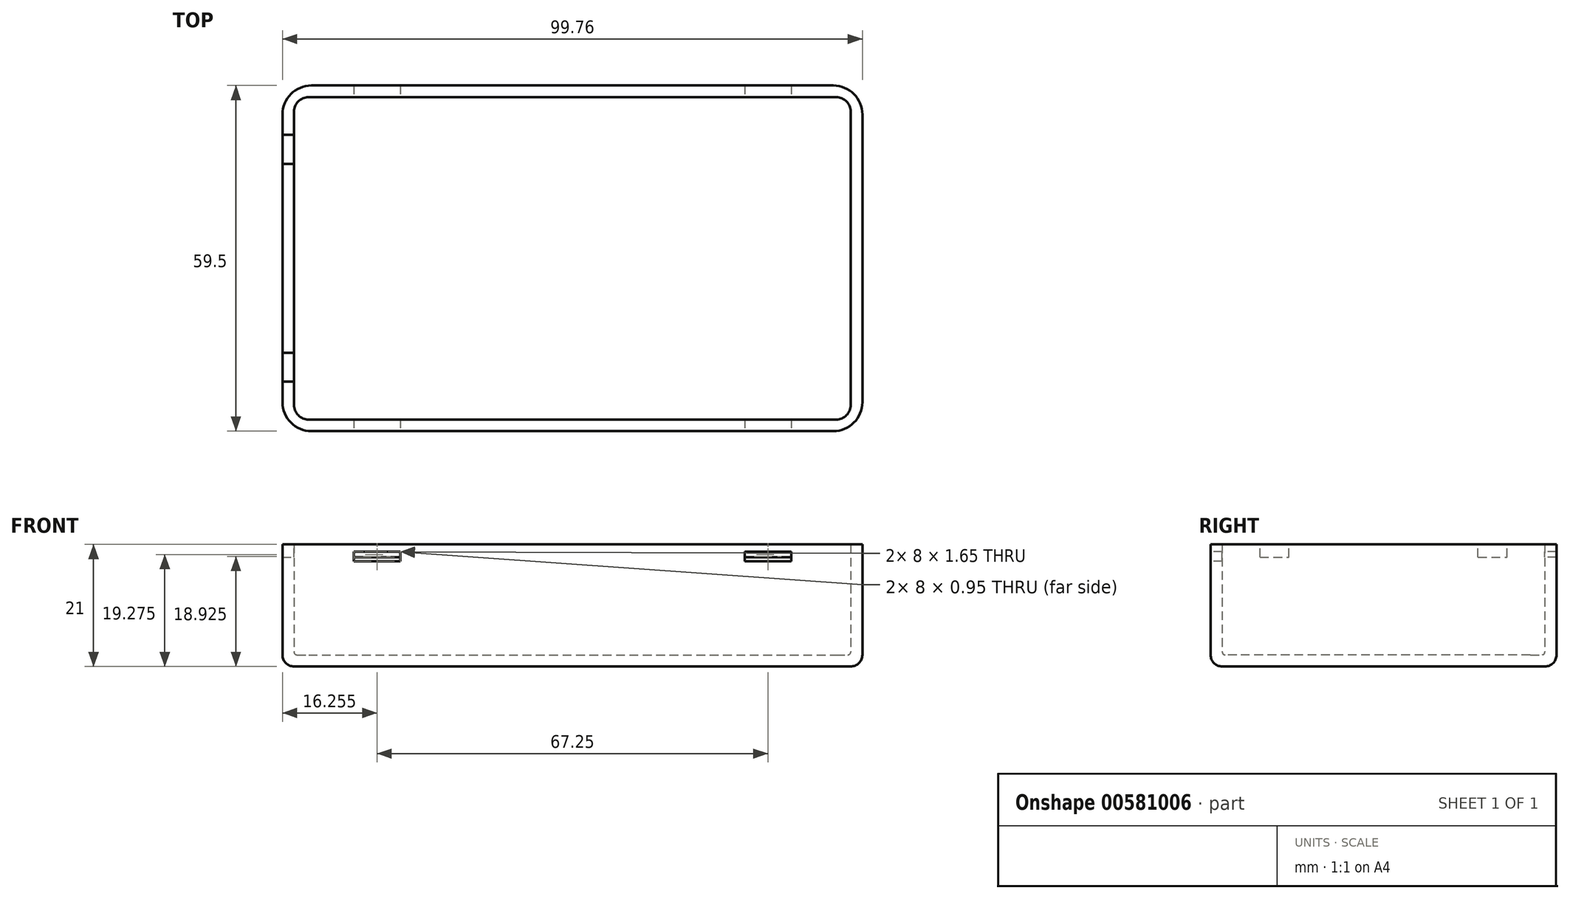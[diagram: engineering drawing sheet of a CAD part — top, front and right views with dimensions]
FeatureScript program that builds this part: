
annotation { "Feature Type Name" : "Feature", "Feature Type Description" : "" }
export const myFeature = defineFeature(function(context is Context, id is Id, definition is map)
    precondition{}
    {
        {
            var Q0;
            Q0=qCreatedBy(makeId("Top.planeOp"),FACE);
            var sketch = newSketch(context, id + "F0", { "sketchPlane" : qUnion([Q0])});
            skLineSegment(sketch, "E0.bottom", {"start": v(44.88, -29.75) * mm, "end": v(-44.88, -29.75) * mm});
            skLineSegment(sketch, "E0.top", {"start": v(44.88, 29.75) * mm, "end": v(-44.88, 29.75) * mm});
            skLineSegment(sketch, "E0.left", {"start": v(49.88, -24.75) * mm, "end": v(49.88, 24.75) * mm});
            skLineSegment(sketch, "E0.right", {"start": v(-49.88, -24.75) * mm, "end": v(-49.88, 24.75) * mm});
            skPoint(sketch, "E0.middle", {"position": v(0, 0) * mm});
            skLineSegment(sketch, "E1.bottom", {"start": v(45.38, -27.75) * mm, "end": v(-45.38, -27.75) * mm});
            skLineSegment(sketch, "E1.top", {"start": v(45.38, 27.75) * mm, "end": v(-45.38, 27.75) * mm});
            skLineSegment(sketch, "E1.left", {"start": v(47.88, -25.25) * mm, "end": v(47.88, 25.25) * mm});
            skLineSegment(sketch, "E1.right", {"start": v(-47.88, -25.25) * mm, "end": v(-47.88, 25.25) * mm});
            skPoint(sketch, "E2.visualSharp", {"position": v(-49.88, 29.75) * mm});
            skArc(sketch, "E2.filletArc", {"start": v(-44.88, 29.75) * mm, "mid": v(-48.41, 28.29) * mm, "end": v(-49.88, 24.75) * mm});
            skPoint(sketch, "E3.visualSharp", {"position": v(-49.88, -29.75) * mm});
            skArc(sketch, "E3.filletArc", {"start": v(-49.88, -24.75) * mm, "mid": v(-48.41, -28.29) * mm, "end": v(-44.88, -29.75) * mm});
            skPoint(sketch, "E4.visualSharp", {"position": v(49.88, 29.75) * mm});
            skArc(sketch, "E4.filletArc", {"start": v(49.87, 24.75) * mm, "mid": v(48.41, 28.29) * mm, "end": v(44.88, 29.75) * mm});
            skPoint(sketch, "E5.visualSharp", {"position": v(49.88, -29.75) * mm});
            skArc(sketch, "E5.filletArc", {"start": v(44.88, -29.75) * mm, "mid": v(48.41, -28.29) * mm, "end": v(49.88, -24.75) * mm});
            skPoint(sketch, "E6.visualSharp", {"position": v(-47.88, 27.75) * mm});
            skArc(sketch, "E6.filletArc", {"start": v(-45.38, 27.75) * mm, "mid": v(-47.14, 27.02) * mm, "end": v(-47.88, 25.25) * mm});
            skPoint(sketch, "E7.visualSharp", {"position": v(47.88, 27.75) * mm});
            skArc(sketch, "E7.filletArc", {"start": v(47.88, 25.25) * mm, "mid": v(47.14, 27.02) * mm, "end": v(45.38, 27.75) * mm});
            skPoint(sketch, "E8.visualSharp", {"position": v(47.88, -27.75) * mm});
            skArc(sketch, "E8.filletArc", {"start": v(45.38, -27.75) * mm, "mid": v(47.14, -27.02) * mm, "end": v(47.88, -25.25) * mm});
            skPoint(sketch, "E9.visualSharp", {"position": v(-47.88, -27.75) * mm});
            skArc(sketch, "E9.filletArc", {"start": v(-47.88, -25.25) * mm, "mid": v(-47.14, -27.02) * mm, "end": v(-45.38, -27.75) * mm});
            skSolve(sketch);
        }
        {
            var Q0;
            Q0=makeQuery(id+"F0.imprint","IMPRINT",FACE,{"disambiguationData":[TD([[makeQuery(id+"F0.imprint","IMPRINT",EDGE,{"derivedFrom":sQuery(id+"F0.wireOp",EDGE,"E0.bottom")}),-1.0]])]});
            var Q1;
            Q1=makeQuery(id+"F0.imprint","IMPRINT",FACE,{"disambiguationData":[TD([[makeQuery(id+"F0.imprint","IMPRINT",EDGE,{"derivedFrom":sQuery(id+"F0.wireOp",EDGE,"E1.bottom")}),-1.0]])]});
            extrude(context, id + "F1", {"entities" : qUnion([Q0, Q1]), "depth" : 2 * mm, "offsetDistance" : 25 * mm});
        }
        {
            var Q0;
            Q0 = qSketchRegion(id + "F0", true);
            extrude(context, id + "F2", {"entities" : qUnion([Q0]), "operationType" : NewBodyOperationType.ADD, "depth" : 21 * mm, "offsetDistance" : 25 * mm});
        }
        {
            var Q0;
            Q0=makeQuery(id+"F1.opExtrude","CAP_EDGE",EDGE,{"disambiguationData":[OSD([sQuery(id+"F0.wireOp",EDGE,"E0.bottom")])],"isStart":true});
            var Q1;
            Q1=makeQuery(id+"F1.opExtrude","CAP_EDGE",EDGE,{"disambiguationData":[OSD([sQuery(id+"F0.wireOp",EDGE,"E3.filletArc")])],"isStart":true});
            var Q2;
            Q2=makeQuery(id+"F1.opExtrude","CAP_EDGE",EDGE,{"disambiguationData":[OSD([sQuery(id+"F0.wireOp",EDGE,"E0.right")])],"isStart":true});
            var Q3;
            Q3=makeQuery(id+"F1.opExtrude","CAP_EDGE",EDGE,{"disambiguationData":[OSD([sQuery(id+"F0.wireOp",EDGE,"E2.filletArc")])],"isStart":true});
            var Q4;
            Q4=makeQuery(id+"F1.opExtrude","CAP_EDGE",EDGE,{"disambiguationData":[OSD([sQuery(id+"F0.wireOp",EDGE,"E0.top")])],"isStart":true});
            var Q5;
            Q5=makeQuery(id+"F1.opExtrude","CAP_EDGE",EDGE,{"disambiguationData":[OSD([sQuery(id+"F0.wireOp",EDGE,"E4.filletArc")])],"isStart":true});
            var Q6;
            Q6=makeQuery(id+"F1.opExtrude","CAP_EDGE",EDGE,{"disambiguationData":[OSD([sQuery(id+"F0.wireOp",EDGE,"E0.left")])],"isStart":true});
            var Q7;
            Q7=makeQuery(id+"F1.opExtrude","CAP_EDGE",EDGE,{"disambiguationData":[OSD([sQuery(id+"F0.wireOp",EDGE,"E5.filletArc")])],"isStart":true});
            fillet(context, id + "F3", {"entities" : qUnion([Q0, Q1, Q2, Q3, Q4, Q5, Q6, Q7]), "radius" : 2 * mm, "tangentPropagation" : true, "allowEdgeOverflow" : false});
        }
        {
            var Q0;
            Q0=makeQuery(id+"F2.opExtrude","CAP_FACE",FACE,{"disambiguationData":[OSD([sQuery(id+"F0.wireOp",EDGE,"E0.bottom"),sQuery(id+"F0.wireOp",EDGE,"E0.top"),sQuery(id+"F0.wireOp",EDGE,"E0.left"),sQuery(id+"F0.wireOp",EDGE,"E0.right"),sQuery(id+"F0.wireOp",EDGE,"E1.bottom"),sQuery(id+"F0.wireOp",EDGE,"E1.top"),sQuery(id+"F0.wireOp",EDGE,"E1.left"),sQuery(id+"F0.wireOp",EDGE,"E1.right"),sQuery(id+"F0.wireOp",EDGE,"E2.filletArc"),sQuery(id+"F0.wireOp",EDGE,"E3.filletArc"),sQuery(id+"F0.wireOp",EDGE,"E4.filletArc"),sQuery(id+"F0.wireOp",EDGE,"E5.filletArc"),sQuery(id+"F0.wireOp",EDGE,"E6.filletArc"),sQuery(id+"F0.wireOp",EDGE,"E7.filletArc"),sQuery(id+"F0.wireOp",EDGE,"E8.filletArc"),sQuery(id+"F0.wireOp",EDGE,"E9.filletArc")])],"isStart":false});
            var sketch = newSketch(context, id + "F4", { "sketchPlane" : qUnion([Q0])});
            skLineSegment(sketch, "E10.bottom", {"start": v(-49.88, 21.25) * mm, "end": v(-47.88, 21.25) * mm});
            skLineSegment(sketch, "E10.top", {"start": v(-49.88, 16.25) * mm, "end": v(-47.88, 16.25) * mm});
            skLineSegment(sketch, "E10.left", {"start": v(-49.88, 21.25) * mm, "end": v(-49.88, 16.25) * mm});
            skLineSegment(sketch, "E10.right", {"start": v(-47.88, 21.25) * mm, "end": v(-47.88, 16.25) * mm});
            skLineSegment(sketch, "E11.bottom", {"start": v(-49.88, -21.25) * mm, "end": v(-47.88, -21.25) * mm});
            skLineSegment(sketch, "E11.top", {"start": v(-49.88, -16.25) * mm, "end": v(-47.88, -16.25) * mm});
            skLineSegment(sketch, "E11.left", {"start": v(-49.88, -21.25) * mm, "end": v(-49.88, -16.25) * mm});
            skLineSegment(sketch, "E11.right", {"start": v(-47.88, -21.25) * mm, "end": v(-47.88, -16.25) * mm});
            skLineSegment(sketch, "E12.bottom", {"start": v(-37.63, 29.75) * mm, "end": v(-29.63, 29.75) * mm});
            skLineSegment(sketch, "E12.top", {"start": v(-37.63, 27.75) * mm, "end": v(-29.63, 27.75) * mm});
            skLineSegment(sketch, "E12.left", {"start": v(-37.63, 29.75) * mm, "end": v(-37.63, 27.75) * mm});
            skLineSegment(sketch, "E12.right", {"start": v(-29.63, 29.75) * mm, "end": v(-29.63, 27.75) * mm});
            skLineSegment(sketch, "E13.bottom", {"start": v(-37.63, -27.75) * mm, "end": v(-29.63, -27.75) * mm});
            skLineSegment(sketch, "E13.top", {"start": v(-37.63, -29.75) * mm, "end": v(-29.63, -29.75) * mm});
            skLineSegment(sketch, "E13.left", {"start": v(-37.63, -27.75) * mm, "end": v(-37.63, -29.75) * mm});
            skLineSegment(sketch, "E13.right", {"start": v(-29.63, -27.75) * mm, "end": v(-29.63, -29.75) * mm});
            skLineSegment(sketch, "E14.bottom", {"start": v(37.63, 29.75) * mm, "end": v(29.62, 29.75) * mm});
            skLineSegment(sketch, "E14.top", {"start": v(37.63, 27.75) * mm, "end": v(29.62, 27.75) * mm});
            skLineSegment(sketch, "E14.left", {"start": v(37.63, 29.75) * mm, "end": v(37.63, 27.75) * mm});
            skLineSegment(sketch, "E14.right", {"start": v(29.62, 29.75) * mm, "end": v(29.62, 27.75) * mm});
            skLineSegment(sketch, "E15.bottom", {"start": v(37.63, -27.75) * mm, "end": v(29.63, -27.75) * mm});
            skLineSegment(sketch, "E15.top", {"start": v(37.63, -29.75) * mm, "end": v(29.63, -29.75) * mm});
            skLineSegment(sketch, "E15.left", {"start": v(37.63, -27.75) * mm, "end": v(37.63, -29.75) * mm});
            skLineSegment(sketch, "E15.right", {"start": v(29.63, -27.75) * mm, "end": v(29.63, -29.75) * mm});
            skLineSegment(sketch, "E16.top", {"start": v(-37.63, 28.4) * mm, "end": v(-29.63, 28.4) * mm});
            skLineSegment(sketch, "E16.left", {"start": v(-37.63, 29.75) * mm, "end": v(-37.63, 28.4) * mm});
            skLineSegment(sketch, "E16.right", {"start": v(-29.63, 29.75) * mm, "end": v(-29.63, 28.4) * mm});
            skLineSegment(sketch, "E17.bottom", {"start": v(29.62, 29.75) * mm, "end": v(37.63, 29.75) * mm});
            skLineSegment(sketch, "E17.top", {"start": v(29.62, 28.4) * mm, "end": v(37.62, 28.4) * mm});
            skLineSegment(sketch, "E17.left", {"start": v(29.62, 29.75) * mm, "end": v(29.62, 28.4) * mm});
            skLineSegment(sketch, "E17.right", {"start": v(37.63, 29.75) * mm, "end": v(37.63, 28.4) * mm});
            skLineSegment(sketch, "E18.bottom", {"start": v(29.63, -29.75) * mm, "end": v(37.63, -29.75) * mm});
            skLineSegment(sketch, "E18.top", {"start": v(29.63, -28.4) * mm, "end": v(37.63, -28.4) * mm});
            skLineSegment(sketch, "E18.left", {"start": v(29.63, -29.75) * mm, "end": v(29.63, -28.4) * mm});
            skLineSegment(sketch, "E18.right", {"start": v(37.63, -29.75) * mm, "end": v(37.63, -28.4) * mm});
            skLineSegment(sketch, "E19.bottom", {"start": v(-37.63, -28.4) * mm, "end": v(-29.63, -28.4) * mm});
            skLineSegment(sketch, "E19.left", {"start": v(-37.63, -28.4) * mm, "end": v(-37.63, -29.75) * mm});
            skLineSegment(sketch, "E19.right", {"start": v(-29.63, -28.4) * mm, "end": v(-29.63, -29.75) * mm});
            skLineSegment(sketch, "E20.bottom", {"start": v(-29.63, -27.75) * mm, "end": v(-37.63, -27.75) * mm});
            skLineSegment(sketch, "E20.top", {"start": v(-29.63, -27.85) * mm, "end": v(-37.63, -27.85) * mm});
            skLineSegment(sketch, "E20.left", {"start": v(-29.63, -27.75) * mm, "end": v(-29.63, -27.85) * mm});
            skLineSegment(sketch, "E20.right", {"start": v(-37.63, -27.75) * mm, "end": v(-37.63, -27.85) * mm});
            skLineSegment(sketch, "E21.top", {"start": v(37.63, -27.85) * mm, "end": v(29.63, -27.85) * mm});
            skLineSegment(sketch, "E21.left", {"start": v(37.63, -27.75) * mm, "end": v(37.63, -27.85) * mm});
            skLineSegment(sketch, "E21.right", {"start": v(29.63, -27.75) * mm, "end": v(29.63, -27.85) * mm});
            skLineSegment(sketch, "E22.top", {"start": v(37.63, 27.85) * mm, "end": v(29.62, 27.85) * mm});
            skLineSegment(sketch, "E22.left", {"start": v(37.63, 27.75) * mm, "end": v(37.63, 27.85) * mm});
            skLineSegment(sketch, "E22.right", {"start": v(29.62, 27.75) * mm, "end": v(29.62, 27.85) * mm});
            skLineSegment(sketch, "E23.bottom", {"start": v(-29.63, 27.75) * mm, "end": v(-37.63, 27.75) * mm});
            skLineSegment(sketch, "E23.top", {"start": v(-29.63, 27.85) * mm, "end": v(-37.63, 27.85) * mm});
            skLineSegment(sketch, "E23.left", {"start": v(-29.63, 27.75) * mm, "end": v(-29.63, 27.85) * mm});
            skLineSegment(sketch, "E23.right", {"start": v(-37.63, 27.75) * mm, "end": v(-37.63, 27.85) * mm});
            skSolve(sketch);
        }
        {
            var Q0;
            Q0=makeQuery(id+"F4.imprint","IMPRINT",FACE,{"disambiguationData":[TD([[makeQuery(id+"F4.imprint","IMPRINT",EDGE,{"derivedFrom":sQuery(id+"F4.wireOp",EDGE,"E11.bottom")}),1.0]])]});
            var Q1;
            Q1=makeQuery(id+"F4.imprint","IMPRINT",FACE,{"disambiguationData":[TD([[makeQuery(id+"F4.imprint","IMPRINT",EDGE,{"derivedFrom":sQuery(id+"F4.wireOp",EDGE,"E10.bottom")}),-1.0]])]});
            var Q2;
            Q2=makeQuery(id+"F4.imprint","IMPRINT",FACE,{"disambiguationData":[TD([[makeQuery(id+"F4.imprint","IMPRINT",EDGE,{"derivedFrom":sQuery(id+"F4.wireOp",EDGE,"E12.left")}),1.0]])]});
            var Q3;
            Q3=makeQuery(id+"F4.imprint","IMPRINT",FACE,{"disambiguationData":[TD([[makeQuery(id+"F4.imprint","IMPRINT",EDGE,{"derivedFrom":sQuery(id+"F4.wireOp",EDGE,"E23.bottom")}),-1.0]])]});
            var Q4;
            Q4=makeQuery(id+"F4.imprint","IMPRINT",FACE,{"disambiguationData":[TD([[makeQuery(id+"F4.imprint","IMPRINT",EDGE,{"derivedFrom":sQuery(id+"F4.wireOp",EDGE,"E14.left")}),-1.0]])]});
            var Q5;
            Q5=makeQuery(id+"F4.imprint","IMPRINT",FACE,{"disambiguationData":[TD([[makeQuery(id+"F4.imprint","IMPRINT",EDGE,{"derivedFrom":sQuery(id+"F4.wireOp",EDGE,"E14.top")}),-1.0]])]});
            extrude(context, id + "F5", {"entities" : qUnion([Q0, Q1, Q2, Q3, Q4, Q5]), "operationType" : NewBodyOperationType.REMOVE, "oppositeDirection" : true, "depth" : 2.2 * mm, "offsetDistance" : 25 * mm});
        }
        {
            var Q0;
            Q0=makeQuery(id+"F1.opExtrude","CAP_FACE",FACE,{"disambiguationData":[OSD([sQuery(id+"F0.wireOp",EDGE,"E0.bottom"),sQuery(id+"F0.wireOp",EDGE,"E0.top"),sQuery(id+"F0.wireOp",EDGE,"E0.left"),sQuery(id+"F0.wireOp",EDGE,"E0.right"),sQuery(id+"F0.wireOp",EDGE,"E2.filletArc"),sQuery(id+"F0.wireOp",EDGE,"E3.filletArc"),sQuery(id+"F0.wireOp",EDGE,"E4.filletArc"),sQuery(id+"F0.wireOp",EDGE,"E5.filletArc")])],"isStart":false});
            fillet(context, id + "F6", {"entities" : qUnion([Q0]), "radius" : 0.5 * mm, "tangentPropagation" : true, "allowEdgeOverflow" : false});
        }
        {
            var Q0;
            Q0=makeQuery(id+"F4.imprint","IMPRINT",FACE,{"disambiguationData":[TD([[makeQuery(id+"F4.imprint","IMPRINT",EDGE,{"derivedFrom":sQuery(id+"F4.wireOp",EDGE,"E13.left")}),1.0]])]});
            var Q1;
            Q1=makeQuery(id+"F4.imprint","IMPRINT",FACE,{"disambiguationData":[TD([[makeQuery(id+"F4.imprint","IMPRINT",EDGE,{"derivedFrom":sQuery(id+"F4.wireOp",EDGE,"E20.bottom")}),1.0]])]});
            var Q2;
            Q2=makeQuery(id+"F4.imprint","IMPRINT",FACE,{"disambiguationData":[TD([[makeQuery(id+"F4.imprint","IMPRINT",EDGE,{"derivedFrom":sQuery(id+"F4.wireOp",EDGE,"E15.bottom")}),1.0]])]});
            var Q3;
            Q3=makeQuery(id+"F4.imprint","IMPRINT",FACE,{"disambiguationData":[TD([[makeQuery(id+"F4.imprint","IMPRINT",EDGE,{"derivedFrom":sQuery(id+"F4.wireOp",EDGE,"E15.left")}),-1.0]])]});
            extrude(context, id + "F7", {"entities" : qUnion([Q0, Q1, Q2, Q3]), "operationType" : NewBodyOperationType.REMOVE, "oppositeDirection" : true, "depth" : 2.9 * mm, "offsetDistance" : 25 * mm});
        }
        {
            var Q0;
            Q0=makeQuery(id+"F4.imprint","IMPRINT",FACE,{"disambiguationData":[TD([[makeQuery(id+"F4.imprint","IMPRINT",EDGE,{"derivedFrom":sQuery(id+"F4.wireOp",EDGE,"E14.left")}),-1.0]])]});
            var Q1;
            Q1=makeQuery(id+"F4.imprint","IMPRINT",FACE,{"disambiguationData":[TD([[makeQuery(id+"F4.imprint","IMPRINT",EDGE,{"derivedFrom":sQuery(id+"F4.wireOp",EDGE,"E12.left")}),1.0]])]});
            var Q2;
            Q2=makeQuery(id+"F4.imprint","IMPRINT",FACE,{"disambiguationData":[TD([[makeQuery(id+"F4.imprint","IMPRINT",EDGE,{"derivedFrom":sQuery(id+"F4.wireOp",EDGE,"E13.left")}),1.0]])]});
            var Q3;
            Q3=makeQuery(id+"F4.imprint","IMPRINT",FACE,{"disambiguationData":[TD([[makeQuery(id+"F4.imprint","IMPRINT",EDGE,{"derivedFrom":sQuery(id+"F4.wireOp",EDGE,"E15.left")}),-1.0]])]});
            extrude(context, id + "F8", {"entities" : qUnion([Q0, Q1, Q2, Q3]), "operationType" : NewBodyOperationType.ADD, "oppositeDirection" : true, "depth" : 1.25 * mm, "offsetDistance" : 25 * mm});
        }
    });
